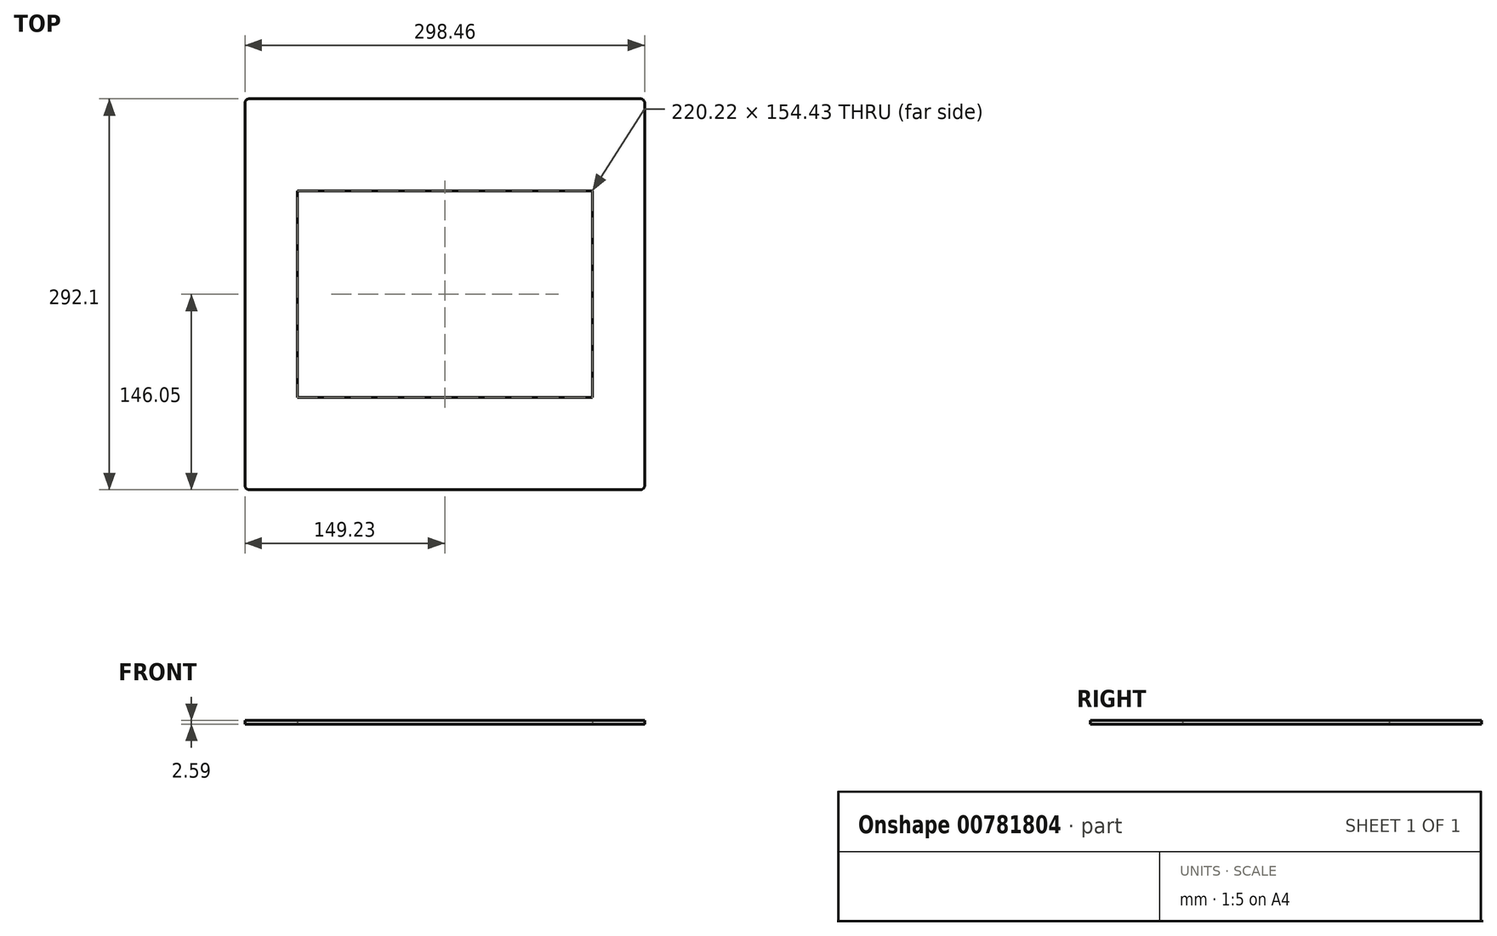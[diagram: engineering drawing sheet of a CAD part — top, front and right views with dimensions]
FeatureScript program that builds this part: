
annotation { "Feature Type Name" : "Feature", "Feature Type Description" : "" }
export const myFeature = defineFeature(function(context is Context, id is Id, definition is map)
    precondition{}
    {
        {
            var Q0;
            Q0=qCreatedBy(makeId("Top.planeOp"),FACE);
            var sketch = newSketch(context, id + "F0", { "sketchPlane" : qUnion([Q0])});
            skLineSegment(sketch, "E0.bottom", {"start": v(-110.1, 77.22) * mm, "end": v(110.1, 77.22) * mm});
            skLineSegment(sketch, "E0.top", {"start": v(-110.1, -77.22) * mm, "end": v(110.1, -77.22) * mm});
            skLineSegment(sketch, "E0.left", {"start": v(-110.1, 77.22) * mm, "end": v(-110.1, -77.22) * mm});
            skLineSegment(sketch, "E0.right", {"start": v(110.1, 77.22) * mm, "end": v(110.1, -77.22) * mm});
            skLineSegment(sketch, "E1.bottom", {"start": v(-146.05, 146.05) * mm, "end": v(146.05, 146.05) * mm});
            skLineSegment(sketch, "E1.top", {"start": v(-146.05, -146.05) * mm, "end": v(146.05, -146.05) * mm});
            skLineSegment(sketch, "E1.left", {"start": v(-149.22, 142.88) * mm, "end": v(-149.22, -142.88) * mm});
            skLineSegment(sketch, "E1.right", {"start": v(149.23, 142.88) * mm, "end": v(149.23, -142.88) * mm});
            skLineSegment(sketch, "E2", {"start": v(-149.22, -146.05) * mm, "end": v(149.23, 146.05) * mm, "construction": true});
            skLineSegment(sketch, "E3", {"start": v(-110.1, 77.22) * mm, "end": v(110.1, -77.22) * mm, "construction": true});
            skPoint(sketch, "E4.visualSharp", {"position": v(-149.22, 146.05) * mm});
            skArc(sketch, "E4.filletArc", {"start": v(-146.05, 146.05) * mm, "mid": v(-148.3, 145.12) * mm, "end": v(-149.22, 142.88) * mm});
            skPoint(sketch, "E5.visualSharp", {"position": v(149.23, 146.05) * mm});
            skArc(sketch, "E5.filletArc", {"start": v(149.23, 142.88) * mm, "mid": v(148.3, 145.12) * mm, "end": v(146.05, 146.05) * mm});
            skPoint(sketch, "E6.visualSharp", {"position": v(149.23, -146.05) * mm});
            skArc(sketch, "E6.filletArc", {"start": v(146.05, -146.05) * mm, "mid": v(148.3, -145.12) * mm, "end": v(149.23, -142.88) * mm});
            skPoint(sketch, "E7.visualSharp", {"position": v(-149.22, -146.05) * mm});
            skArc(sketch, "E7.filletArc", {"start": v(-149.22, -142.88) * mm, "mid": v(-148.3, -145.12) * mm, "end": v(-146.05, -146.05) * mm});
            skSolve(sketch);
        }
        {
            var Q0;
            Q0 = qSketchRegion(id + "F0", true);
            extrude(context, id + "F1", {"entities" : qUnion([Q0]), "depth" : 2.59 * mm, "offsetDistance" : 25.4 * mm});
        }
    });
